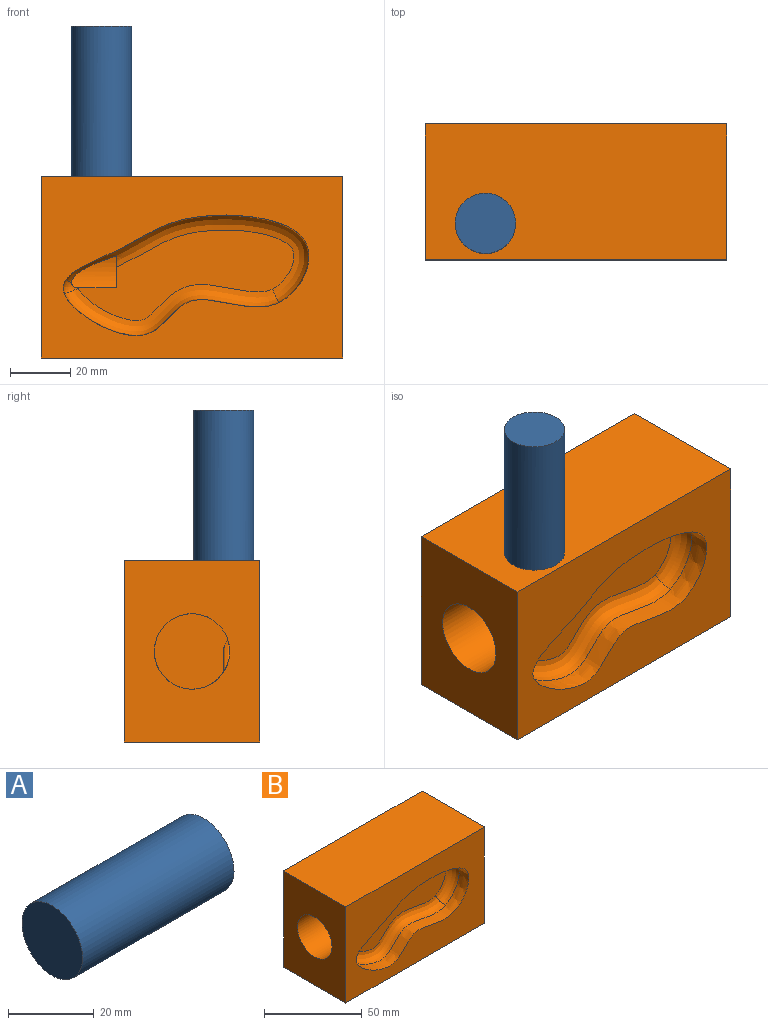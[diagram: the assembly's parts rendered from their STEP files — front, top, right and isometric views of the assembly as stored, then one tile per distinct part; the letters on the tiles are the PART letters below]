
ASSEMBLY  parts=2 mates=1
PART A: 3 faces, bbox 50x20x20 mm
  f0: plane 20x20mm, normal (1,0,0), area 314.2mm2, adj f1
  f1: cylinder r=10mm len=50mm, axis (-1,0,0), area 3141.6mm2, adj f0,f2
  f2: plane 20x20mm, normal (-1,0,0), area 314.2mm2, adj f1
PART B: 14 faces, bbox 100.1x45.1x60.1 mm
  f0: bspline ~5x4.46mm, area 0mm2, adj f8,f11,f12
  f1: plane 100x60mm, normal (0,-1,0), area 3901.5mm2, adj f2,f3,f4,f5,f7
  f2: plane 100x45mm, normal (0,0,1), area 4500mm2, adj f1,f3,f5,f6
  f3: plane 60x45mm, normal (-1,0,0), area 2209.1mm2, adj f1,f2,f4,f6,f12
  f4: plane 100x45mm, normal (0,0,-1), area 4500mm2, adj f1,f3,f5,f6
  f5: plane 60x45mm, normal (1,0,0), area 2700mm2, adj f1,f2,f4,f6
  f6: plane 100x60mm, normal (0,1,0), area 6000mm2, adj f2,f3,f4,f5
  f7: extruded ~81.4x39.97mm, area 1374.7mm2, adj f1,f9,f10,f11
  f8: plane 71.4x30.02mm, normal (0,-1,0), area 1144.4mm2, adj f0,f9,f10,f12,f13
  f9: bspline ~71.33x16.96mm, area 606.5mm2, adj f7,f8,f10,f11
  f10: bspline ~80.74x37.02mm, area 769.1mm2, adj f7,f8,f9,f11,f12,f13
  f11: bspline ~5.04x5mm, area 24.3mm2, adj f0,f7,f9,f10,f12
  f12: cylinder r=12.5mm len=25mm, axis (-1,0,0), area 1846.3mm2, adj f0,f3,f8,f10,f11,f13
  f13: plane 25.14x24.53mm, normal (-1,0,0), area 476.4mm2, adj f8,f10,f12
PLACE A rot(axis=(0,1,0),90deg) t=(-10,-20.5,85)mm
PLACE B t=(0,-10,0)mm
MATE planar A.f1 <-> B.f2  axis (0,0,-1) through (20,-33,60)mm
